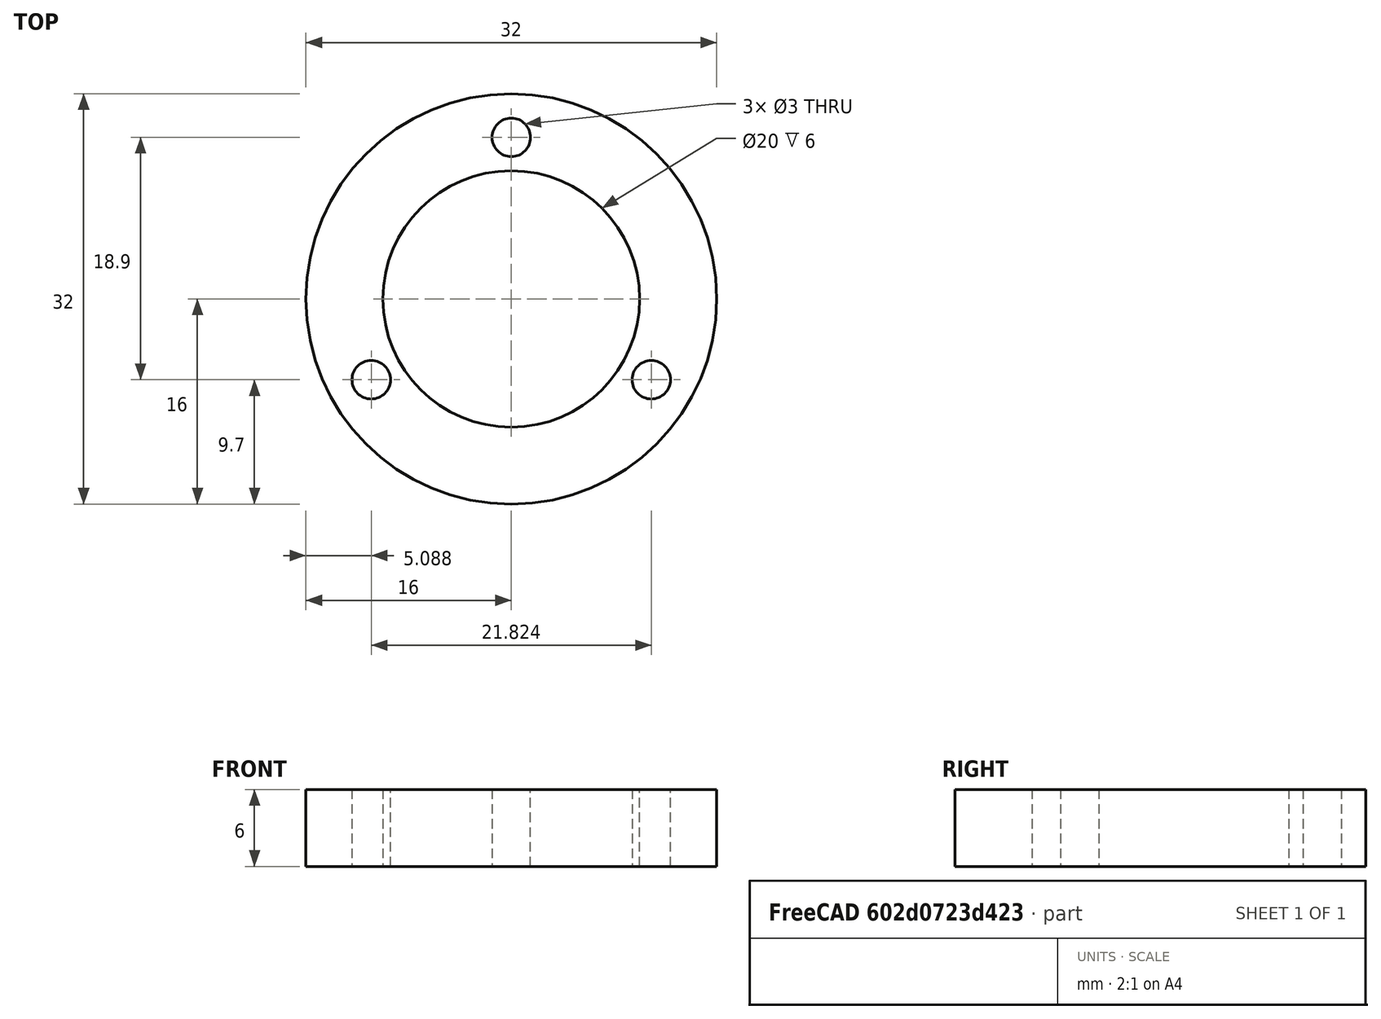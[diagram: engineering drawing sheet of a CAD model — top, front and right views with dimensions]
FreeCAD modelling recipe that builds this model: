
FCSTD DOCUMENT  (FreeCAD 0.16R6707 (Git))
Label: bague_bille
License: All rights reserved
LicenseURL: http://en.wikipedia.org/wiki/All_rights_reserved
objects: Sketcher::SketchObject×1, PartDesign::Pad×1
note: 3 computed .brp shape members not serialized (recipe doc carries the construction recipe); baked Part::Feature solids carry a one-line shape summary decoded from their .brp

FEATURE [Sketcher::SketchObject] Sketch
  sketch-geometry (8):
    g0: Circle CenterX=0 CenterY=0 CenterZ=0 NormalX=0 NormalY=0 NormalZ=1 Radius=16
    g1: Circle CenterX=0 CenterY=0 CenterZ=0 NormalX=0 NormalY=0 NormalZ=1 Radius=10
    g2: GeomPoint [constr] X=0 Y=12.6 Z=0
    g3: GeomPoint [constr] X=10.9119 Y=-6.3 Z=0
    g4: GeomPoint [constr] X=-10.9119 Y=-6.3 Z=0
    g5: Circle CenterX=0 CenterY=12.6 CenterZ=0 NormalX=0 NormalY=0 NormalZ=1 Radius=1.5
    g6: Circle CenterX=10.9119 CenterY=-6.3 CenterZ=0 NormalX=0 NormalY=0 NormalZ=1 Radius=1.5
    g7: Circle CenterX=-10.9119 CenterY=-6.3 CenterZ=0 NormalX=0 NormalY=0 NormalZ=1 Radius=1.5
  constraints (10):
    c: Coincident(g0,g-1)
    c: Coincident(g1,g-1)
    c: Radius(g1) = 10
    c: Radius(g0) = 16
    c: Coincident(g5,g2)
    c: Coincident(g6,g3)
    c: Coincident(g7,g4)
    c: Radius(g5) = 1.5
    c: Equal(g5,g7)
    c: Equal(g5,g6)
FEATURE [PartDesign::Pad] Pad
  Length = 6
  Length2 = 100
  Sketch = -> Sketch
  Type = 0
